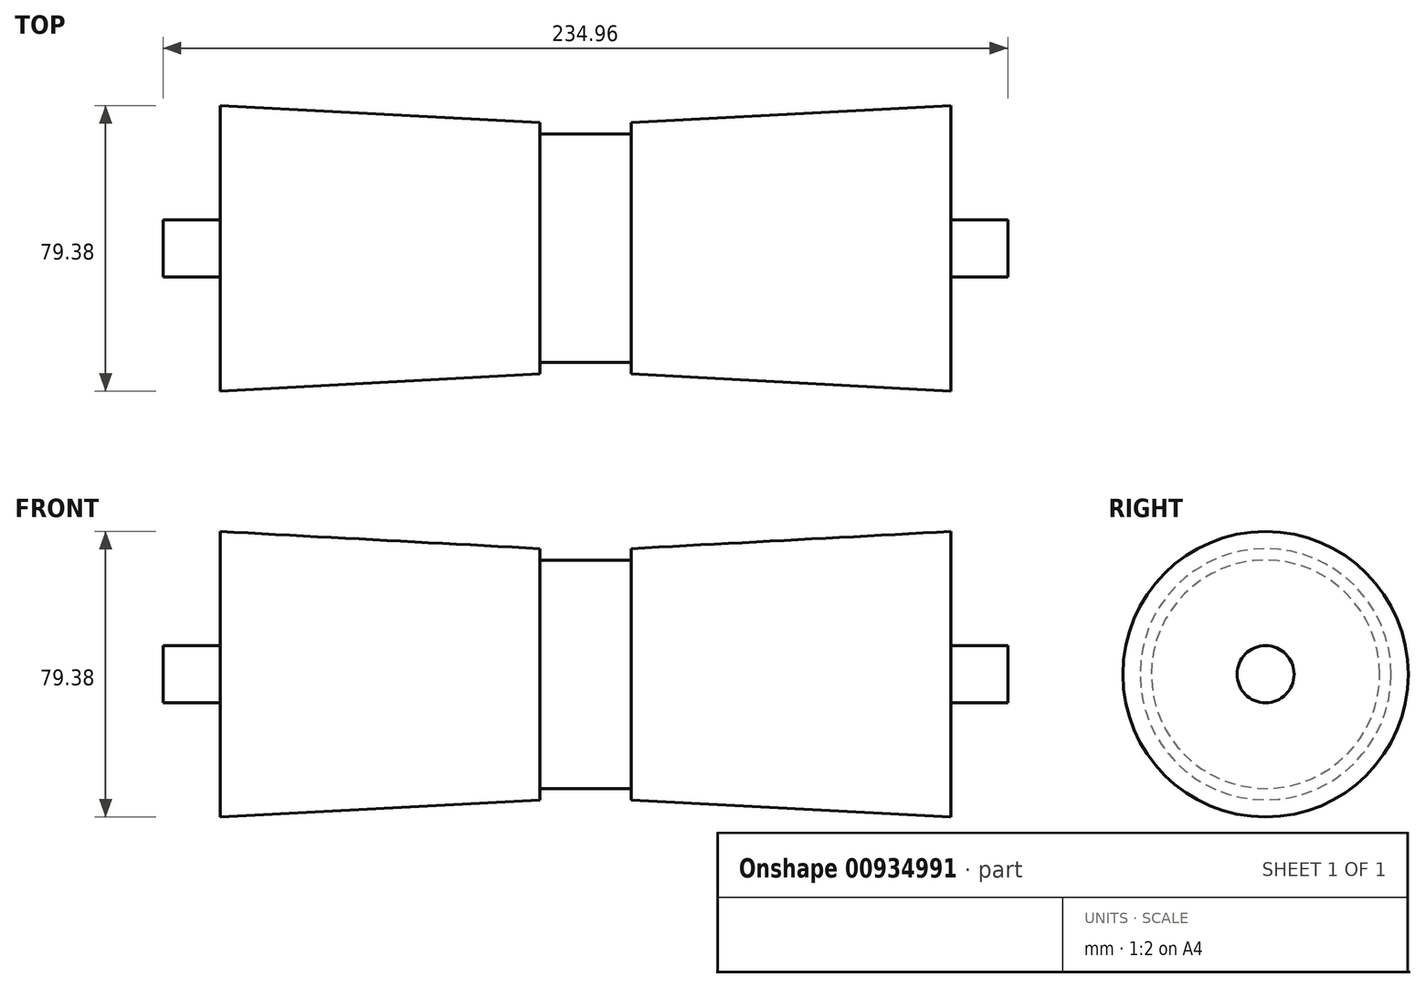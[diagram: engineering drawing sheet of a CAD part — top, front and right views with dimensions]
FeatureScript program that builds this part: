
annotation { "Feature Type Name" : "Feature", "Feature Type Description" : "" }
export const myFeature = defineFeature(function(context is Context, id is Id, definition is map)
    precondition{}
    {
        {
            var Q0;
            Q0=qCreatedBy(makeId("Front.planeOp"),FACE);
            var sketch = newSketch(context, id + "F0", { "sketchPlane" : qUnion([Q0])});
            skLineSegment(sketch, "E0", {"start": v(-101.6, 0) * mm, "end": v(101.6, 0) * mm});
            skLineSegment(sketch, "E1", {"start": v(101.6, 0) * mm, "end": v(101.6, 39.69) * mm});
            skLineSegment(sketch, "E2", {"start": v(101.6, 39.69) * mm, "end": v(12.7, 34.92) * mm});
            skLineSegment(sketch, "E3", {"start": v(12.7, 34.92) * mm, "end": v(12.7, 31.75) * mm});
            skLineSegment(sketch, "E4", {"start": v(12.7, 31.75) * mm, "end": v(-12.7, 31.75) * mm});
            skLineSegment(sketch, "E5", {"start": v(-12.7, 31.75) * mm, "end": v(-12.7, 34.92) * mm});
            skLineSegment(sketch, "E6", {"start": v(-12.7, 34.92) * mm, "end": v(-101.6, 39.69) * mm});
            skLineSegment(sketch, "E7", {"start": v(-101.6, 39.69) * mm, "end": v(-101.6, 0) * mm});
            skSolve(sketch);
        }
        {
            var Q0;
            Q0 = qSketchRegion(id + "F0", true);
            var Q1;
            Q1=sQuery(id+"F0.wireOp",EDGE,"E0");
            revolve(context, id + "F1", {"surfaceOperationType" : NewSurfaceOperationType.NEW, "entities" : qUnion([Q0]), "axis" : qUnion([Q1]), "revolveType" : RevolveType.FULL});
        }
        {
            var Q0;
            Q0=qCreatedBy(makeId("Right.planeOp"),FACE);
            var sketch = newSketch(context, id + "F2", { "sketchPlane" : qUnion([Q0])});
            skCircle(sketch, "E8", {"center": v(0, 0) * mm, "radius": 7.94 * mm});
            skSolve(sketch);
        }
        {
            var Q0;
            Q0 = qSketchRegion(id + "F2", true);
            extrude(context, id + "F3", {"entities" : qUnion([Q0]), "operationType" : NewBodyOperationType.ADD, "depth" : 234.95 * mm, "offsetDistance" : 25.4 * mm, "symmetric" : true});
        }
    });
